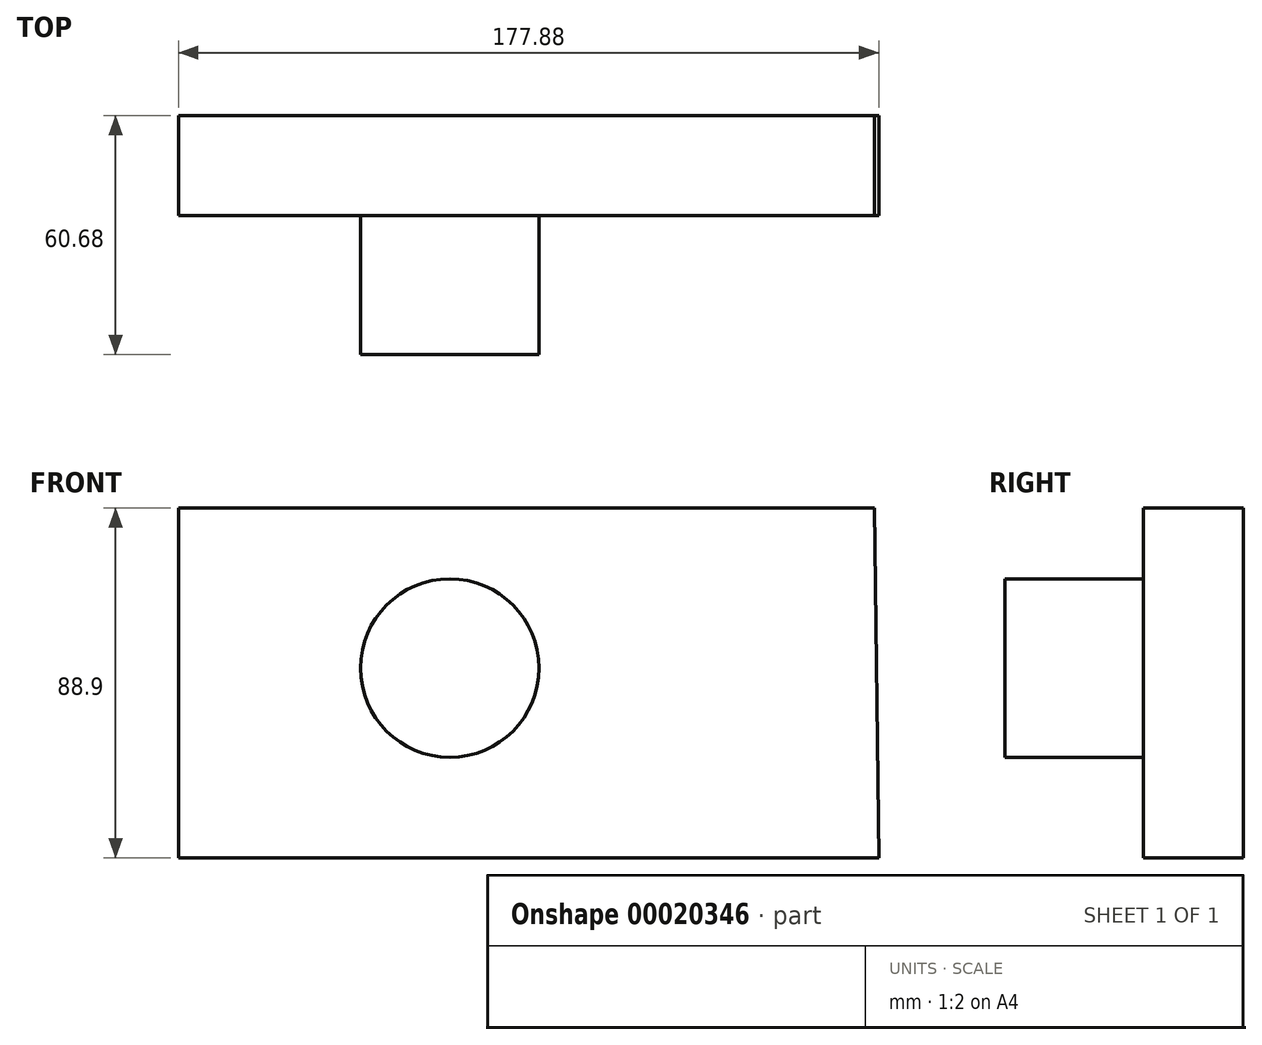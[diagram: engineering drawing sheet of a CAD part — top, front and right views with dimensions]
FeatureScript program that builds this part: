
annotation { "Feature Type Name" : "Feature", "Feature Type Description" : "" }
export const myFeature = defineFeature(function(context is Context, id is Id, definition is map)
    precondition{}
    {
        {
            var Q0;
            Q0=qCreatedBy(makeId("Front.planeOp"),FACE);
            var sketch = newSketch(context, id + "F0", { "sketchPlane" : qUnion([Q0])});
            skLineSegment(sketch, "E0", {"start": v(-87.8, 88.9) * mm, "end": v(-87.8, 0) * mm});
            skLineSegment(sketch, "E1", {"start": v(-87.8, 0) * mm, "end": v(90.08, 0) * mm});
            skLineSegment(sketch, "E2", {"start": v(-87.8, 88.9) * mm, "end": v(88.93, 88.9) * mm});
            skLineSegment(sketch, "E3", {"start": v(88.93, 88.9) * mm, "end": v(90.08, 0) * mm});
            skSolve(sketch);
        }
        {
            var Q0;
            Q0=makeQuery(id+"F0.imprint","IMPRINT",FACE,{"disambiguationData":[TD([[makeQuery(id+"F0.imprint","IMPRINT",EDGE,{"derivedFrom":sQuery(id+"F0.wireOp",EDGE,"E0")}),1.0]])]});
            extrude(context, id + "F1", {"entities" : qUnion([Q0]), "depth" : 25.4 * mm});
        }
        {
            var Q0;
            Q0=makeQuery(id+"F1.opExtrude","CAP_FACE",FACE,{"disambiguationData":[OSD([sQuery(id+"F0.wireOp",EDGE,"E0"),sQuery(id+"F0.wireOp",EDGE,"E1"),sQuery(id+"F0.wireOp",EDGE,"E2"),sQuery(id+"F0.wireOp",EDGE,"E3")])],"isStart":false});
            var sketch = newSketch(context, id + "F2", { "sketchPlane" : qUnion([Q0])});
            skCircle(sketch, "E4", {"center": v(-18.9, 48.21) * mm, "radius": 22.67 * mm});
            skSolve(sketch);
        }
        {
            var Q0;
            Q0 = qSketchRegion(id + "F2", true);
            extrude(context, id + "F3", {"entities" : qUnion([Q0]), "operationType" : NewBodyOperationType.ADD, "depth" : 35.28 * mm});
        }
    });
